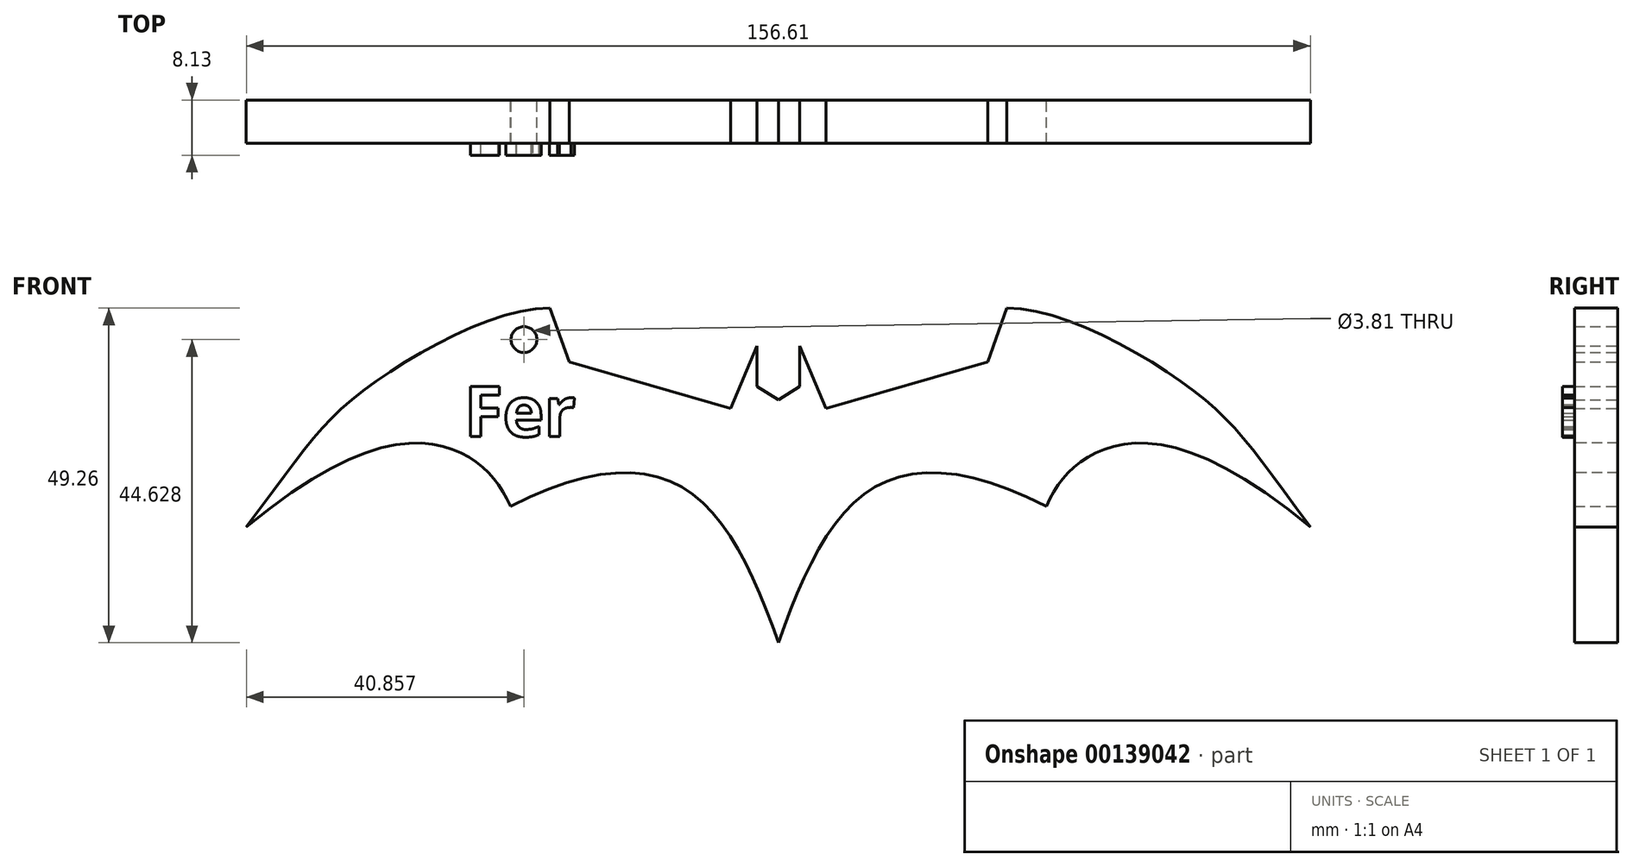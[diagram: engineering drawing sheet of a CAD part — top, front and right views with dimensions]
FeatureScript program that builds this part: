
annotation { "Feature Type Name" : "Feature", "Feature Type Description" : "" }
export const myFeature = defineFeature(function(context is Context, id is Id, definition is map)
    precondition{}
    {
        {
            var Q0;
            Q0=qCreatedBy(makeId("Front.planeOp"),FACE);
            var sketch = newSketch(context, id + "F0", { "sketchPlane" : qUnion([Q0])});
            skLineSegment(sketch, "E0", {"start": v(0.81, -22.94) * mm, "end": v(0.81, 12.8) * mm});
            skLineSegment(sketch, "E1", {"start": v(0.81, 12.8) * mm, "end": v(3.95, 14.75) * mm});
            skLineSegment(sketch, "E2", {"start": v(3.95, 14.75) * mm, "end": v(3.95, 20.77) * mm});
            skLineSegment(sketch, "E3", {"start": v(3.95, 20.77) * mm, "end": v(7.83, 11.56) * mm});
            skLineSegment(sketch, "E4", {"start": v(7.83, 11.56) * mm, "end": v(31.61, 18.42) * mm});
            skLineSegment(sketch, "E5", {"start": v(31.61, 18.42) * mm, "end": v(34.43, 26.32) * mm});
            skFitSpline(sketch, "E6", {"points": [v(34.43, 26.32) * mm, v(61.5, 14.47) * mm, v(79.12, -5.94) * mm], "startDerivative": vector(45.9, 0.7) * mm, "endDerivative": vector(51.14, -68.63) * mm});
            skFitSpline(sketch, "E7", {"points": [v(0.81, -22.94) * mm, v(14.18, -0.55) * mm, v(40.24, -2.85) * mm], "startDerivative": vector(20.43, 57.16) * mm, "endDerivative": vector(67.5, -34.6) * mm});
            skFitSpline(sketch, "E8", {"points": [v(40.24, -2.85) * mm, v(46.18, 4.24) * mm, v(79.12, -5.94) * mm], "startDerivative": vector(11.74, 26.13) * mm, "endDerivative": vector(81.37, -67.95) * mm});
            skLineSegment(sketch, "E9.MirrorCS", {"start": v(-6.21, 11.56) * mm, "end": v(-30, 18.42) * mm});
            skLineSegment(sketch, "E10.MirrorCS", {"start": v(0.81, 12.8) * mm, "end": v(-2.33, 14.75) * mm});
            skLineSegment(sketch, "E11.MirrorCS", {"start": v(-2.33, 14.75) * mm, "end": v(-2.33, 20.77) * mm});
            skLineSegment(sketch, "E12.MirrorCS", {"start": v(-2.33, 20.77) * mm, "end": v(-6.21, 11.56) * mm});
            skFitSpline(sketch, "E13.MirrorCS", {"points": [v(0.81, -22.94) * mm, v(-12.56, -0.55) * mm, v(-38.62, -2.85) * mm], "startDerivative": vector(-20.43, 57.16) * mm, "endDerivative": vector(-67.5, -34.6) * mm});
            skFitSpline(sketch, "E14.MirrorCS", {"points": [v(-38.62, -2.85) * mm, v(-44.56, 4.24) * mm, v(-77.5, -5.94) * mm], "startDerivative": vector(-11.74, 26.13) * mm, "endDerivative": vector(-81.37, -67.95) * mm});
            skFitSpline(sketch, "E15.MirrorCS", {"points": [v(-32.8, 26.32) * mm, v(-59.87, 14.47) * mm, v(-77.5, -5.94) * mm], "startDerivative": vector(-45.9, 0.7) * mm, "endDerivative": vector(-51.14, -68.63) * mm});
            skLineSegment(sketch, "E16.MirrorCS", {"start": v(-30, 18.42) * mm, "end": v(-32.8, 26.32) * mm});
            skCircle(sketch, "E17", {"center": v(-36.63, 21.69) * mm, "radius": 1.9 * mm});
            skSolve(sketch);
        }
        {
            var Q0;
            Q0=makeQuery(id+"F0.imprint","IMPRINT",FACE,{"disambiguationData":[TD([[makeQuery(id+"F0.imprint","IMPRINT",EDGE,{"derivedFrom":sQuery(id+"F0.wireOp",EDGE,"E0")}),-1.0]])]});
            var Q1;
            Q1=makeQuery(id+"F0.imprint","IMPRINT",FACE,{"disambiguationData":[TD([[makeQuery(id+"F0.imprint","IMPRINT",EDGE,{"derivedFrom":sQuery(id+"F0.wireOp",EDGE,"E0")}),1.0]])]});
            extrude(context, id + "F1", {"entities" : qUnion([Q0, Q1]), "depth" : 6.35 * mm});
        }
        {
            var Q0;
            Q0=makeQuery(id+"F1.opExtrude","CAP_FACE",FACE,{"disambiguationData":[OSD([sQuery(id+"F0.wireOp",EDGE,"E1"),sQuery(id+"F0.wireOp",EDGE,"E2"),sQuery(id+"F0.wireOp",EDGE,"E3"),sQuery(id+"F0.wireOp",EDGE,"E4"),sQuery(id+"F0.wireOp",EDGE,"E5"),sQuery(id+"F0.wireOp",EDGE,"E6"),sQuery(id+"F0.wireOp",EDGE,"E7"),sQuery(id+"F0.wireOp",EDGE,"E8"),sQuery(id+"F0.wireOp",EDGE,"E9.MirrorCS"),sQuery(id+"F0.wireOp",EDGE,"E10.MirrorCS"),sQuery(id+"F0.wireOp",EDGE,"E11.MirrorCS"),sQuery(id+"F0.wireOp",EDGE,"E12.MirrorCS"),sQuery(id+"F0.wireOp",EDGE,"E13.MirrorCS"),sQuery(id+"F0.wireOp",EDGE,"E14.MirrorCS"),sQuery(id+"F0.wireOp",EDGE,"E15.MirrorCS"),sQuery(id+"F0.wireOp",EDGE,"E16.MirrorCS"),sQuery(id+"F0.wireOp",EDGE,"E17")])],"isStart":false});
            var sketch = newSketch(context, id + "F2", { "sketchPlane" : qUnion([Q0])});
            skText(sketch, "E18", { "text": "Fer", "fontName": "OpenSans-Bold.ttf"});
            const initialGuessF2  = {"E18": [-0.04542, 0.0074, 1, 0, 0.00742]};
            skSetInitialGuess(sketch, initialGuessF2);
            skSolve(sketch);
        }
        {
            var Q0;
            Q0 = qSketchRegion(id + "F2", true);
            extrude(context, id + "F3", {"entities" : qUnion([Q0]), "operationType" : NewBodyOperationType.ADD, "depth" : 1.78 * mm});
        }
    });
